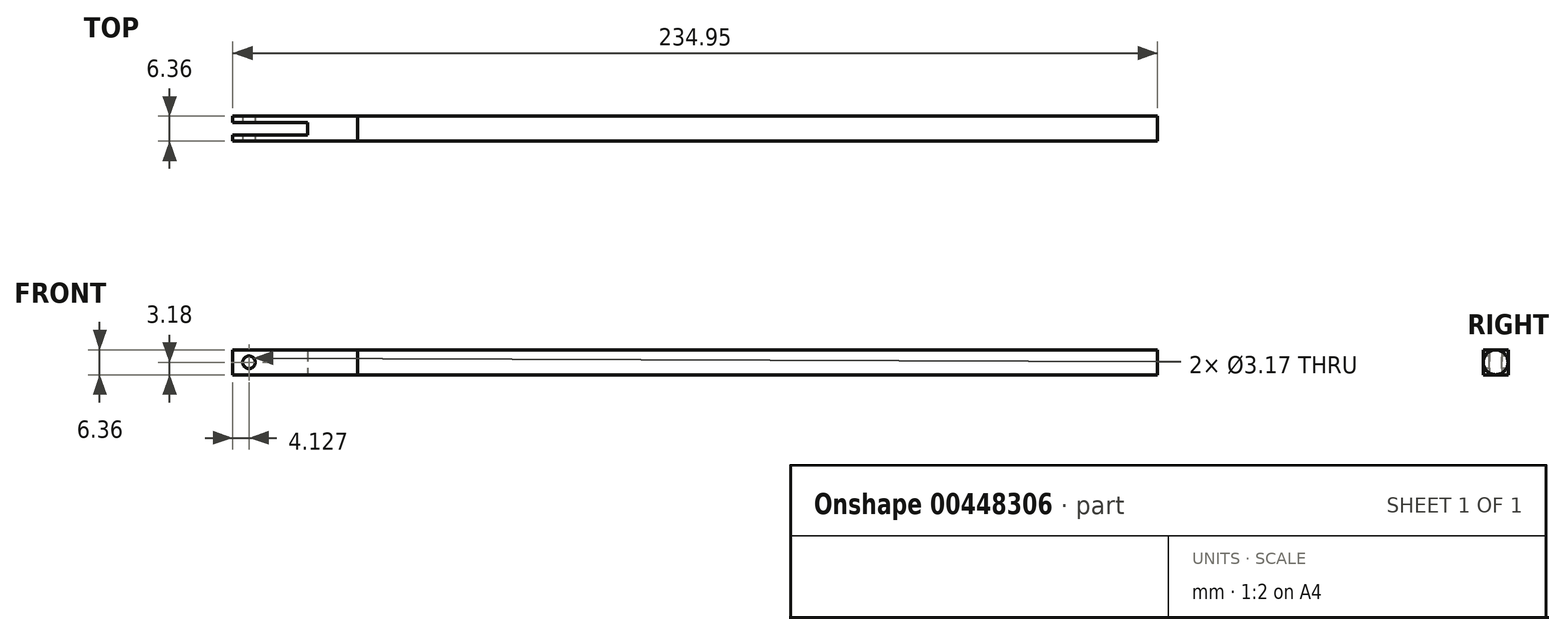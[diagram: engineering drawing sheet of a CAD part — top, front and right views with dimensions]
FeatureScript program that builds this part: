
annotation { "Feature Type Name" : "Feature", "Feature Type Description" : "" }
export const myFeature = defineFeature(function(context is Context, id is Id, definition is map)
    precondition{}
    {
        {
            var Q0;
            Q0=qCreatedBy(makeId("Front.planeOp"),FACE);
            var sketch = newSketch(context, id + "F0", { "sketchPlane" : qUnion([Q0])});
            skLineSegment(sketch, "E0.bottom", {"start": v(101.6, 3.18) * mm, "end": v(-101.6, 3.18) * mm});
            skLineSegment(sketch, "E0.top", {"start": v(101.6, -3.17) * mm, "end": v(-101.6, -3.17) * mm});
            skLineSegment(sketch, "E0.left", {"start": v(101.6, 3.18) * mm, "end": v(101.6, -3.17) * mm});
            skLineSegment(sketch, "E0.right", {"start": v(-101.6, 3.18) * mm, "end": v(-101.6, -3.17) * mm});
            skPoint(sketch, "E0.middle", {"position": v(0, 0) * mm});
            skLineSegment(sketch, "E1", {"start": v(-101.6, 0) * mm, "end": v(101.6, 0) * mm});
            skSolve(sketch);
        }
        {
            var Q0;
            {var subQ0=sQuery(id+"F0.wireOp",EDGE,"E0.bottom");Q0=makeQuery(id+"F0.imprint","IMPRINT",FACE,{"disambiguationData":[TD([[makeQuery(id+"F0.imprint","IMPRINT",EDGE,{"derivedFrom":subQ0}),1.0]])]});}
            var Q1;
            Q1=sQuery(id+"F0.wireOp",EDGE,"E1");
            revolve(context, id + "F1", {"entities" : qUnion([Q0]), "axis" : qUnion([Q1]), "revolveType" : RevolveType.FULL});
        }
        {
            var Q0;
            Q0=makeQuery(id+"F1.opRevolve","SWEPT_FACE",FACE,{"disambiguationData":[OSD([sQuery(id+"F0.wireOp",EDGE,"E0.right")])]});
            var sketch = newSketch(context, id + "F2", { "sketchPlane" : qUnion([Q0])});
            skLineSegment(sketch, "E2.bottom", {"start": v(3.18, -3.17) * mm, "end": v(-3.17, -3.17) * mm});
            skLineSegment(sketch, "E2.top", {"start": v(3.17, 3.18) * mm, "end": v(-3.18, 3.18) * mm});
            skLineSegment(sketch, "E2.left", {"start": v(3.18, -3.17) * mm, "end": v(3.17, 3.18) * mm});
            skLineSegment(sketch, "E2.right", {"start": v(-3.17, -3.17) * mm, "end": v(-3.18, 3.18) * mm});
            skPoint(sketch, "E2.middle", {"position": v(0, 0) * mm});
            skSolve(sketch);
        }
        {
            var Q0;
            Q0 = qSketchRegion(id + "F2", true);
            extrude(context, id + "F3", {"entities" : qUnion([Q0]), "operationType" : NewBodyOperationType.ADD, "depth" : 12.7 * mm});
        }
        {
            var Q0;
            Q0=makeQuery(id+"F3.opExtrude","CAP_FACE",FACE,{"disambiguationData":[OSD([sQuery(id+"F2.wireOp",EDGE,"E2.bottom"),sQuery(id+"F2.wireOp",EDGE,"E2.top"),sQuery(id+"F2.wireOp",EDGE,"E2.left"),sQuery(id+"F2.wireOp",EDGE,"E2.right")])],"isStart":false});
            var sketch = newSketch(context, id + "F4", { "sketchPlane" : qUnion([Q0])});
            skLineSegment(sketch, "E3.bottom", {"start": v(3.17, 3.18) * mm, "end": v(1.59, 3.18) * mm});
            skLineSegment(sketch, "E3.top", {"start": v(3.17, -3.17) * mm, "end": v(1.59, -3.17) * mm});
            skLineSegment(sketch, "E3.left", {"start": v(3.17, 3.18) * mm, "end": v(3.17, -3.17) * mm});
            skLineSegment(sketch, "E3.right", {"start": v(1.59, 3.18) * mm, "end": v(1.59, -3.17) * mm});
            skLineSegment(sketch, "E4.bottom", {"start": v(-1.59, 3.18) * mm, "end": v(-3.17, 3.18) * mm});
            skLineSegment(sketch, "E4.top", {"start": v(-1.59, -3.17) * mm, "end": v(-3.17, -3.17) * mm});
            skLineSegment(sketch, "E4.left", {"start": v(-1.59, 3.18) * mm, "end": v(-1.59, -3.17) * mm});
            skLineSegment(sketch, "E4.right", {"start": v(-3.17, 3.18) * mm, "end": v(-3.17, -3.17) * mm});
            skSolve(sketch);
        }
        {
            var Q0;
            Q0 = qSketchRegion(id + "F4", true);
            extrude(context, id + "F5", {"entities" : qUnion([Q0]), "operationType" : NewBodyOperationType.ADD, "depth" : 19.05 * mm});
        }
        {
            var Q0;
            Q0=makeQuery(id+"F5.boolean.opBoolean","MERGE",FACE,{"derivedFrom":[makeQuery(id+"F3.opExtrude","SWEPT_FACE",FACE,{"disambiguationData":[OSD([sQuery(id+"F2.wireOp",EDGE,"E2.left")])]}),makeQuery(id+"F5.opExtrude","SWEPT_FACE",FACE,{"disambiguationData":[OSD([sQuery(id+"F4.wireOp",EDGE,"E3.left")])]})]});
            var sketch = newSketch(context, id + "F6", { "sketchPlane" : qUnion([Q0])});
            skCircle(sketch, "E5", {"center": v(-129.22, 0) * mm, "radius": 1.59 * mm});
            skSolve(sketch);
        }
        {
            var Q0;
            Q0 = qSketchRegion(id + "F6", true);
            extrude(context, id + "F7", {"entities" : qUnion([Q0]), "operationType" : NewBodyOperationType.REMOVE, "oppositeDirection" : true, "depth" : 25.4 * mm});
        }
    });
